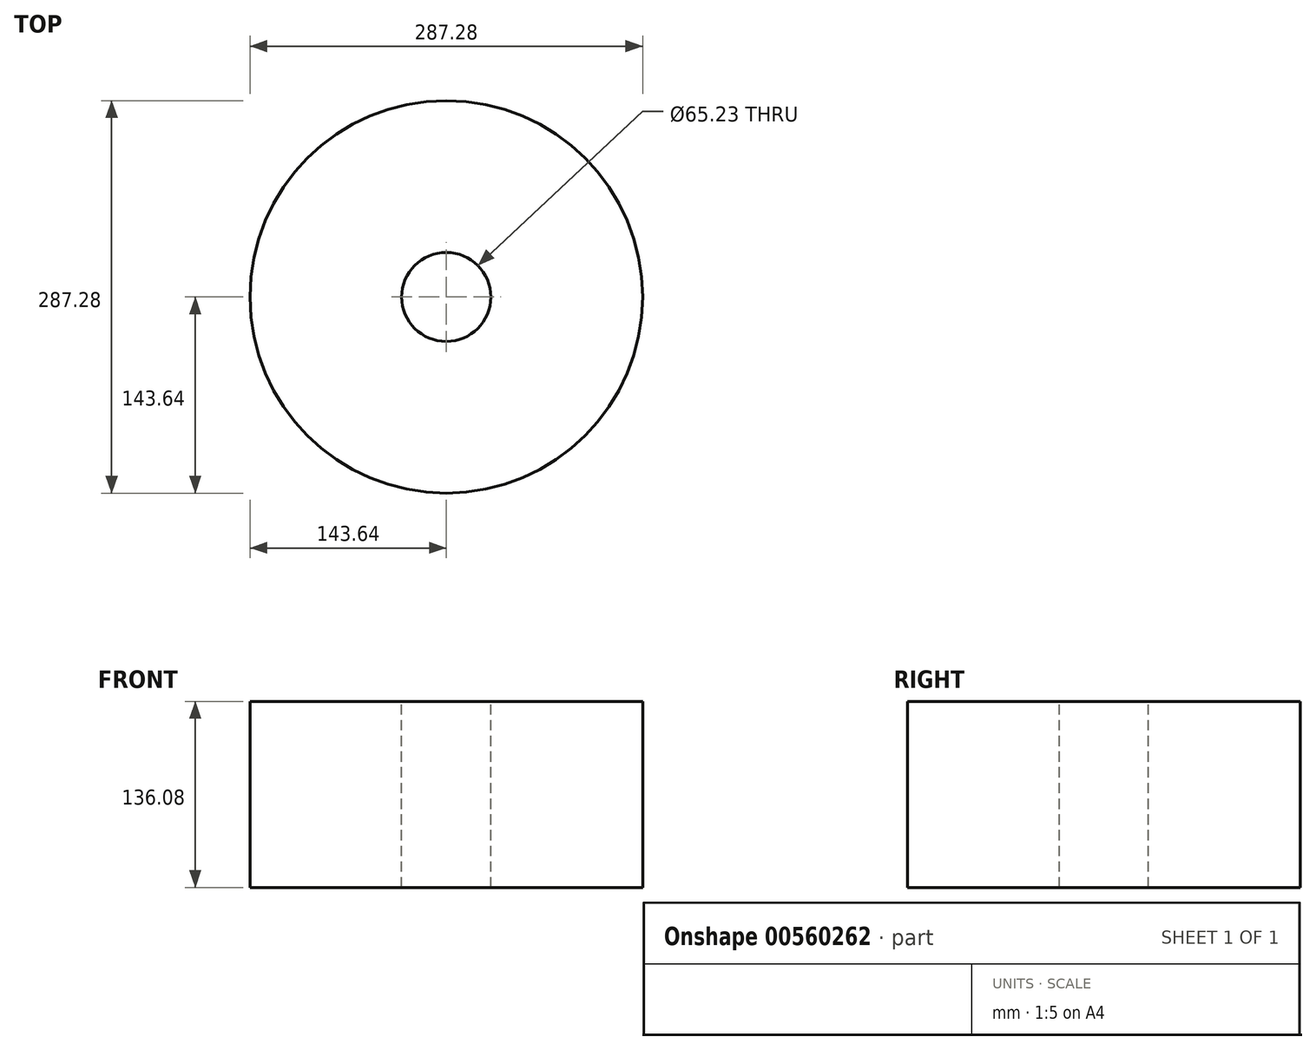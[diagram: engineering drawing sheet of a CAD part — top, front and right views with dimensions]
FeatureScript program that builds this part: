
annotation { "Feature Type Name" : "Feature", "Feature Type Description" : "" }
export const myFeature = defineFeature(function(context is Context, id is Id, definition is map)
    precondition{}
    {
        {
            var Q0;
            Q0=qCreatedBy(makeId("Top.planeOp"),FACE);
            var sketch = newSketch(context, id + "F0", { "sketchPlane" : qUnion([Q0])});
            skCircle(sketch, "E0", {"center": v(0, 0) * mm, "radius": 143.64 * mm});
            skCircle(sketch, "E1", {"center": v(0, 0) * mm, "radius": 32.61 * mm});
            skSolve(sketch);
        }
        {
            var Q0;
            Q0 = qSketchRegion(id + "F0", true);
            extrude(context, id + "F1", {"entities" : qUnion([Q0]), "oppositeDirection" : true, "depth" : 136.08 * mm, "offsetDistance" : 25 * mm});
        }
    });
